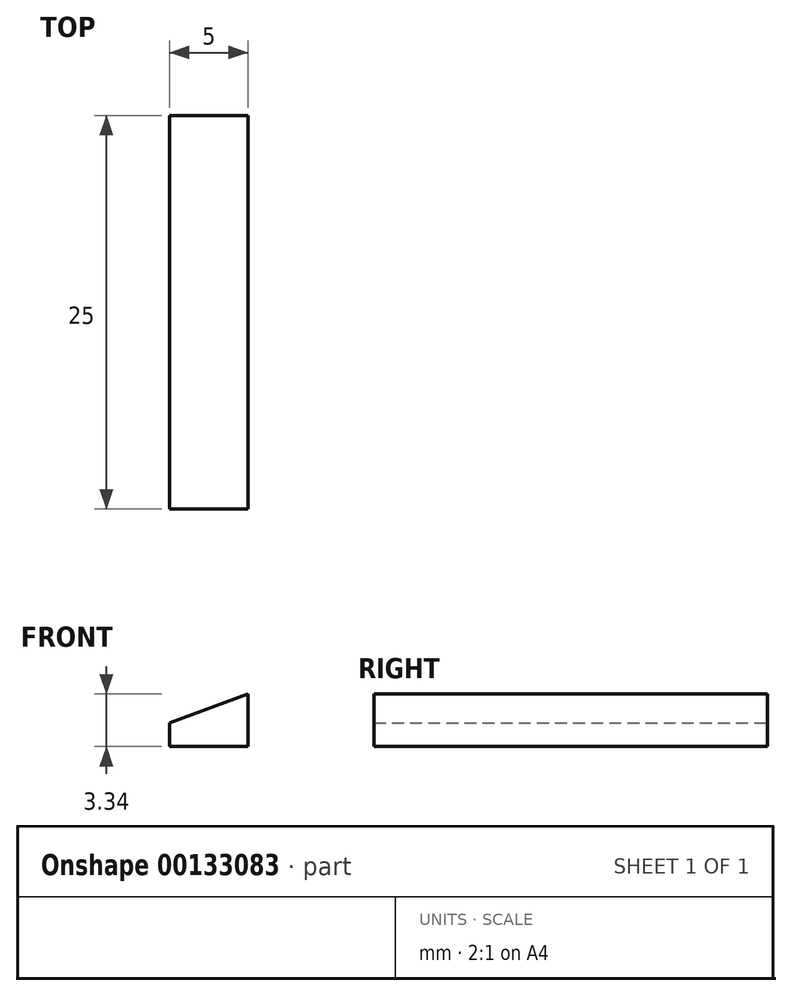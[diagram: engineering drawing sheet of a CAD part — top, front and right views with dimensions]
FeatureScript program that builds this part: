
annotation { "Feature Type Name" : "Feature", "Feature Type Description" : "" }
export const myFeature = defineFeature(function(context is Context, id is Id, definition is map)
    precondition{}
    {
        {
            var Q0;
            Q0=qCreatedBy(makeId("Front.planeOp"),FACE);
            var sketch = newSketch(context, id + "F0", { "sketchPlane" : qUnion([Q0])});
            skLineSegment(sketch, "E0.bottom", {"start": v(24.26, 22.62) * mm, "end": v(-25.74, 22.62) * mm});
            skLineSegment(sketch, "E0.top", {"start": v(24.26, -27.38) * mm, "end": v(-25.74, -27.38) * mm});
            skLineSegment(sketch, "E0.left", {"start": v(24.26, 22.62) * mm, "end": v(24.26, -27.38) * mm});
            skLineSegment(sketch, "E0.right", {"start": v(-25.74, 22.62) * mm, "end": v(-25.74, -27.38) * mm});
            skPoint(sketch, "E0.middle", {"position": v(-0.74, -2.38) * mm});
            skLineSegment(sketch, "E1", {"start": v(-25.74, -2.38) * mm, "end": v(-0.74, -2.38) * mm});
            skLineSegment(sketch, "E2", {"start": v(-25.74, 22.62) * mm, "end": v(-10.74, 22.62) * mm});
            skLineSegment(sketch, "E3", {"start": v(24.26, 22.62) * mm, "end": v(24.26, 7.62) * mm});
            skLineSegment(sketch, "E4", {"start": v(24.26, -27.38) * mm, "end": v(14.26, -27.38) * mm});
            skLineSegment(sketch, "E5", {"start": v(-10.74, 22.62) * mm, "end": v(-10.74, 7.62) * mm});
            skLineSegment(sketch, "E6", {"start": v(-10.74, 7.62) * mm, "end": v(-0.74, 7.62) * mm});
            skLineSegment(sketch, "E7", {"start": v(-0.74, 7.62) * mm, "end": v(-0.74, -2.38) * mm});
            skLineSegment(sketch, "E8", {"start": v(-25.74, -2.38) * mm, "end": v(-25.74, -12.38) * mm});
            skLineSegment(sketch, "E9", {"start": v(-0.74, -2.38) * mm, "end": v(-0.74, -17.38) * mm});
            skLineSegment(sketch, "E10", {"start": v(-0.74, -17.38) * mm, "end": v(-0.74, -2.38) * mm});
            skLineSegment(sketch, "E11", {"start": v(-0.74, -17.38) * mm, "end": v(-10.74, -17.38) * mm});
            skLineSegment(sketch, "E12", {"start": v(-10.74, -17.38) * mm, "end": v(-25.74, -12.38) * mm});
            skLineSegment(sketch, "E13", {"start": v(14.26, -27.38) * mm, "end": v(14.26, -17.38) * mm});
            skLineSegment(sketch, "E14", {"start": v(-0.74, -12.38) * mm, "end": v(6.76, -12.38) * mm});
            skLineSegment(sketch, "E15", {"start": v(6.76, -12.38) * mm, "end": v(6.76, -17.38) * mm});
            skLineSegment(sketch, "E16", {"start": v(6.76, -17.38) * mm, "end": v(14.26, -17.38) * mm});
            skLineSegment(sketch, "E17", {"start": v(-5.74, 7.62) * mm, "end": v(-0.74, 7.62) * mm});
            skLineSegment(sketch, "E18", {"start": v(-5.74, 11.62) * mm, "end": v(24.26, 22.62) * mm});
            skLineSegment(sketch, "E19", {"start": v(24.26, 7.62) * mm, "end": v(24.26, 2.62) * mm});
            skLineSegment(sketch, "E20", {"start": v(24.26, 2.62) * mm, "end": v(4.26, 2.62) * mm});
            skLineSegment(sketch, "E21", {"start": v(4.26, 2.62) * mm, "end": v(-0.74, -2.38) * mm});
            skPoint(sketch, "E22.endSnap0", {"position": v(-5.74, 10.12) * mm});
            skLineSegment(sketch, "E23", {"start": v(-5.74, 11.62) * mm, "end": v(-5.74, 10.12) * mm});
            skLineSegment(sketch, "E24", {"start": v(-5.74, 10.12) * mm, "end": v(-3.24, 10.12) * mm});
            skPoint(sketch, "E24.endSnap0", {"position": v(-3.24, 7.62) * mm});
            skLineSegment(sketch, "E25", {"start": v(-3.24, 10.12) * mm, "end": v(-0.74, 10.12) * mm});
            skLineSegment(sketch, "E26", {"start": v(-0.74, 10.12) * mm, "end": v(-0.74, 7.62) * mm});
            skLineSegment(sketch, "E27", {"start": v(-0.74, 7.62) * mm, "end": v(-0.74, 13.46) * mm});
            skLineSegment(sketch, "E28", {"start": v(4.26, 2.62) * mm, "end": v(-0.74, 2.62) * mm});
            skSolve(sketch);
        }
        {
            var Q0;
            {var subQ0=sQuery(id+"F0.wireOp",EDGE,"E3");Q0=makeQuery(id+"F0.imprint","IMPRINT",FACE,{"disambiguationData":[TD([[makeQuery(id+"F0.imprint","IMPRINT",EDGE,{"derivedFrom":subQ0}),-1.0]])]});}
            var Q1;
            {var subQ1=sQuery(id+"F0.wireOp",EDGE,"E23");Q1=makeQuery(id+"F0.imprint","IMPRINT",FACE,{"disambiguationData":[TD([[makeQuery(id+"F0.imprint","IMPRINT",EDGE,{"derivedFrom":subQ1}),1.0]])]});}
            extrude(context, id + "F1", {"entities" : qUnion([Q0, Q1]), "depth" : 25 * mm});
        }
    });
